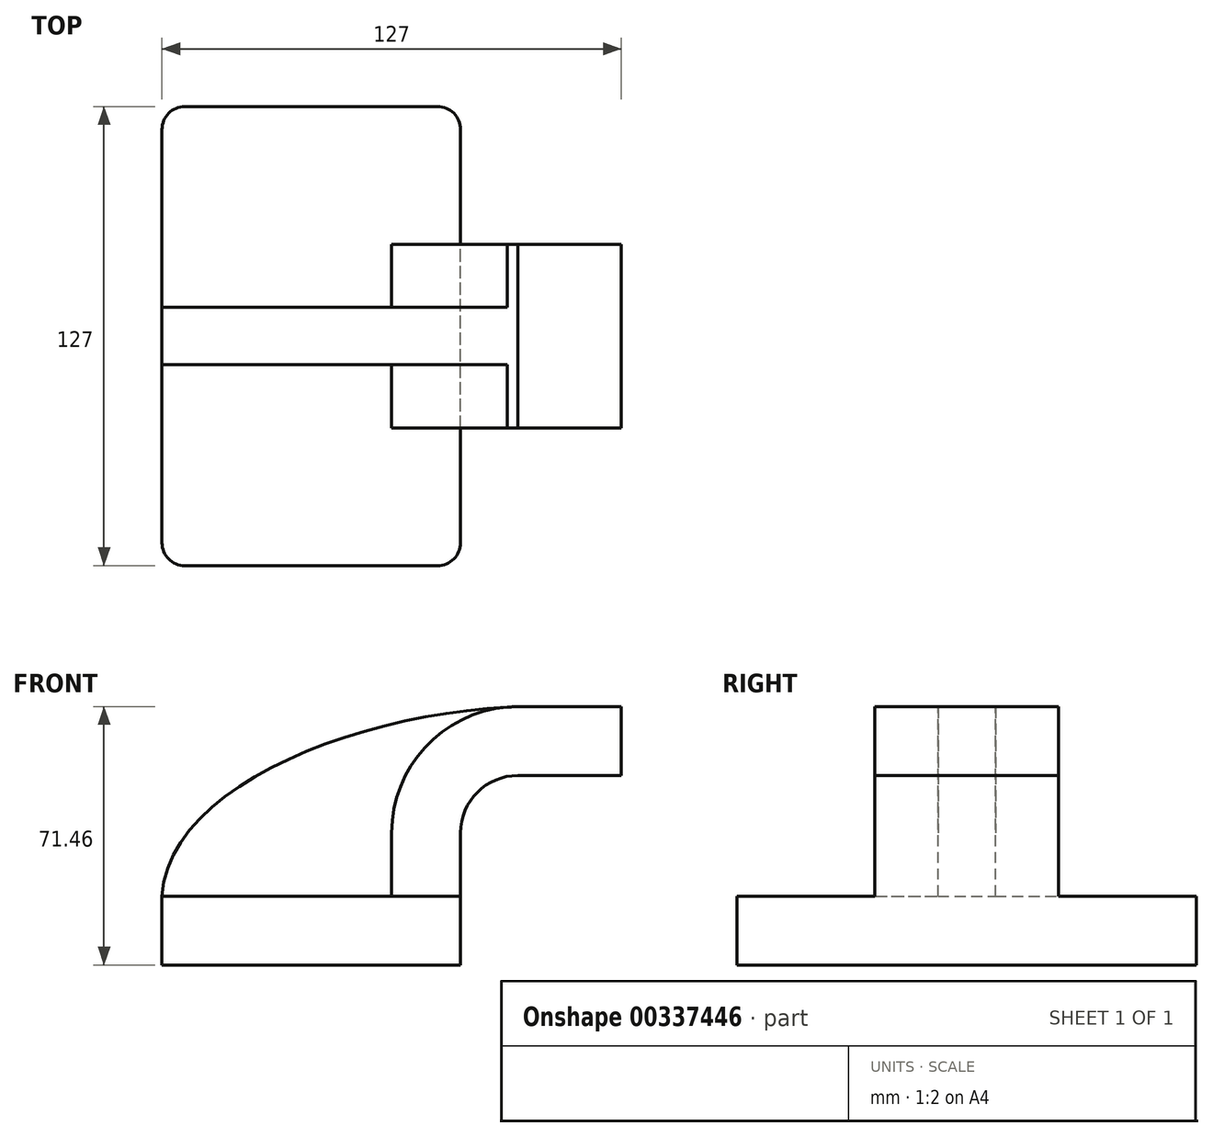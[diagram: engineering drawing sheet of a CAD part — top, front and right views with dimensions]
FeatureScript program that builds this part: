
annotation { "Feature Type Name" : "Feature", "Feature Type Description" : "" }
export const myFeature = defineFeature(function(context is Context, id is Id, definition is map)
    precondition{}
    {
        {
            var Q0;
            Q0=qCreatedBy(makeId("Front.planeOp"),FACE);
            var sketch = newSketch(context, id + "F0", { "sketchPlane" : qUnion([Q0])});
            skLineSegment(sketch, "E0.bottom", {"start": v(41.28, -9.52) * mm, "end": v(-41.28, -9.53) * mm});
            skLineSegment(sketch, "E0.top", {"start": v(41.28, 9.53) * mm, "end": v(-41.28, 9.53) * mm});
            skLineSegment(sketch, "E0.left", {"start": v(41.28, -9.52) * mm, "end": v(41.28, 9.53) * mm});
            skLineSegment(sketch, "E0.right", {"start": v(-41.28, -9.53) * mm, "end": v(-41.28, 9.53) * mm});
            skPoint(sketch, "E0.middle", {"position": v(0, 0) * mm});
            skLineSegment(sketch, "E1.bottom", {"start": v(111.13, 38.1) * mm, "end": v(60.33, 38.1) * mm});
            skLineSegment(sketch, "E1.top", {"start": v(111.13, 66.68) * mm, "end": v(60.33, 66.68) * mm});
            skLineSegment(sketch, "E1.left", {"start": v(111.13, 38.1) * mm, "end": v(111.13, 66.68) * mm});
            skLineSegment(sketch, "E1.right", {"start": v(60.33, 38.1) * mm, "end": v(60.33, 66.68) * mm});
            skPoint(sketch, "E1.middle", {"position": v(85.72, 52.39) * mm});
            skLineSegment(sketch, "E2", {"start": v(41.28, 9.53) * mm, "end": v(41.28, 27) * mm});
            skArc(sketch, "E3", {"start": v(41.27, 27) * mm, "mid": v(45.92, 38.23) * mm, "end": v(57.15, 42.88) * mm});
            skLineSegment(sketch, "E4", {"start": v(57.15, 42.88) * mm, "end": v(85.72, 42.88) * mm});
            skLineSegment(sketch, "E5.0", {"start": v(57.15, 61.93) * mm, "end": v(85.72, 61.93) * mm});
            skArc(sketch, "E5.1", {"start": v(22.23, 27) * mm, "mid": v(32.45, 51.7) * mm, "end": v(57.15, 61.93) * mm});
            skLineSegment(sketch, "E5.2", {"start": v(22.22, 9.53) * mm, "end": v(22.22, 27) * mm});
            skLineSegment(sketch, "E6", {"start": v(85.73, 38.1) * mm, "end": v(85.73, 66.68) * mm});
            skFitSpline(sketch, "E7", {"points": [v(-41.28, 9.52) * mm, v(57.15, 61.93) * mm], "startDerivative": vector(5.86, 93.1) * mm, "endDerivative": vector(128.83, 4.2) * mm});
            skSolve(sketch);
        }
        {
            var Q0;
            Q0=makeQuery(id+"F0.imprint","IMPRINT",FACE,{"disambiguationData":[TD([[makeQuery(id+"F0.imprint","IMPRINT",EDGE,{"derivedFrom":sQuery(id+"F0.wireOp",EDGE,"E0.bottom")}),-1.0]])]});
            extrude(context, id + "F1", {"entities" : qUnion([Q0]), "endBound" : BoundingType.SYMMETRIC, "depth" : 127 * mm});
        }
        {
            var Q0;
            {var subQ1=sQuery(id+"F0.wireOp",EDGE,"E2");Q0=makeQuery(id+"F0.imprint","IMPRINT",FACE,{"disambiguationData":[TD([[makeQuery(id+"F0.imprint","IMPRINT",EDGE,{"derivedFrom":subQ1}),1.0]])]});}
            var Q1;
            {var subQ0=sQuery(id+"F0.wireOp",EDGE,"E4");var subQ1=sQuery(id+"F0.wireOp",EDGE,"E1.right");var subQ2=makeQuery(id+"F0.imprint","INTERSECT",VERTEX,{"derivedFrom":[subQ1,subQ0]});Q1=makeQuery(id+"F0.imprint","IMPRINT",FACE,{"disambiguationData":[TD([[makeQuery(id+"F0.imprint","IMPRINT",EDGE,{"disambiguationData":[TD([[subQ2,-1.0]])],"derivedFrom":subQ1}),-1.0]])]});}
            extrude(context, id + "F2", {"entities" : qUnion([Q0, Q1]), "operationType" : NewBodyOperationType.ADD, "endBound" : BoundingType.SYMMETRIC, "depth" : 50.8 * mm});
        }
        {
            var Q0;
            {var subQ3=sQuery(id+"F0.wireOp",EDGE,"E5.2");Q0=makeQuery(id+"F0.imprint","IMPRINT",FACE,{"disambiguationData":[TD([[makeQuery(id+"F0.imprint","IMPRINT",EDGE,{"derivedFrom":subQ3}),1.0]])]});}
            extrude(context, id + "F3", {"entities" : qUnion([Q0]), "operationType" : NewBodyOperationType.ADD, "endBound" : BoundingType.SYMMETRIC, "depth" : 15.88 * mm});
        }
        {
            var Q0;
            Q0=makeQuery(id+"F1.opExtrude","CAP_EDGE",EDGE,{"disambiguationData":[OSD([sQuery(id+"F0.wireOp",EDGE,"E0.left")])],"isStart":false});
            var Q1;
            Q1=makeQuery(id+"F1.opExtrude","CAP_EDGE",EDGE,{"disambiguationData":[OSD([sQuery(id+"F0.wireOp",EDGE,"E0.right")])],"isStart":false});
            var Q2;
            Q2=makeQuery(id+"F1.opExtrude","CAP_EDGE",EDGE,{"disambiguationData":[OSD([sQuery(id+"F0.wireOp",EDGE,"E0.left")])],"isStart":true});
            var Q3;
            Q3=makeQuery(id+"F1.opExtrude","CAP_EDGE",EDGE,{"disambiguationData":[OSD([sQuery(id+"F0.wireOp",EDGE,"E0.right")])],"isStart":true});
            fillet(context, id + "F4", {"entities" : qUnion([Q0, Q1, Q2, Q3]), "radius" : 6.35 * mm, "tangentPropagation" : true, "allowEdgeOverflow" : false});
        }
    });
